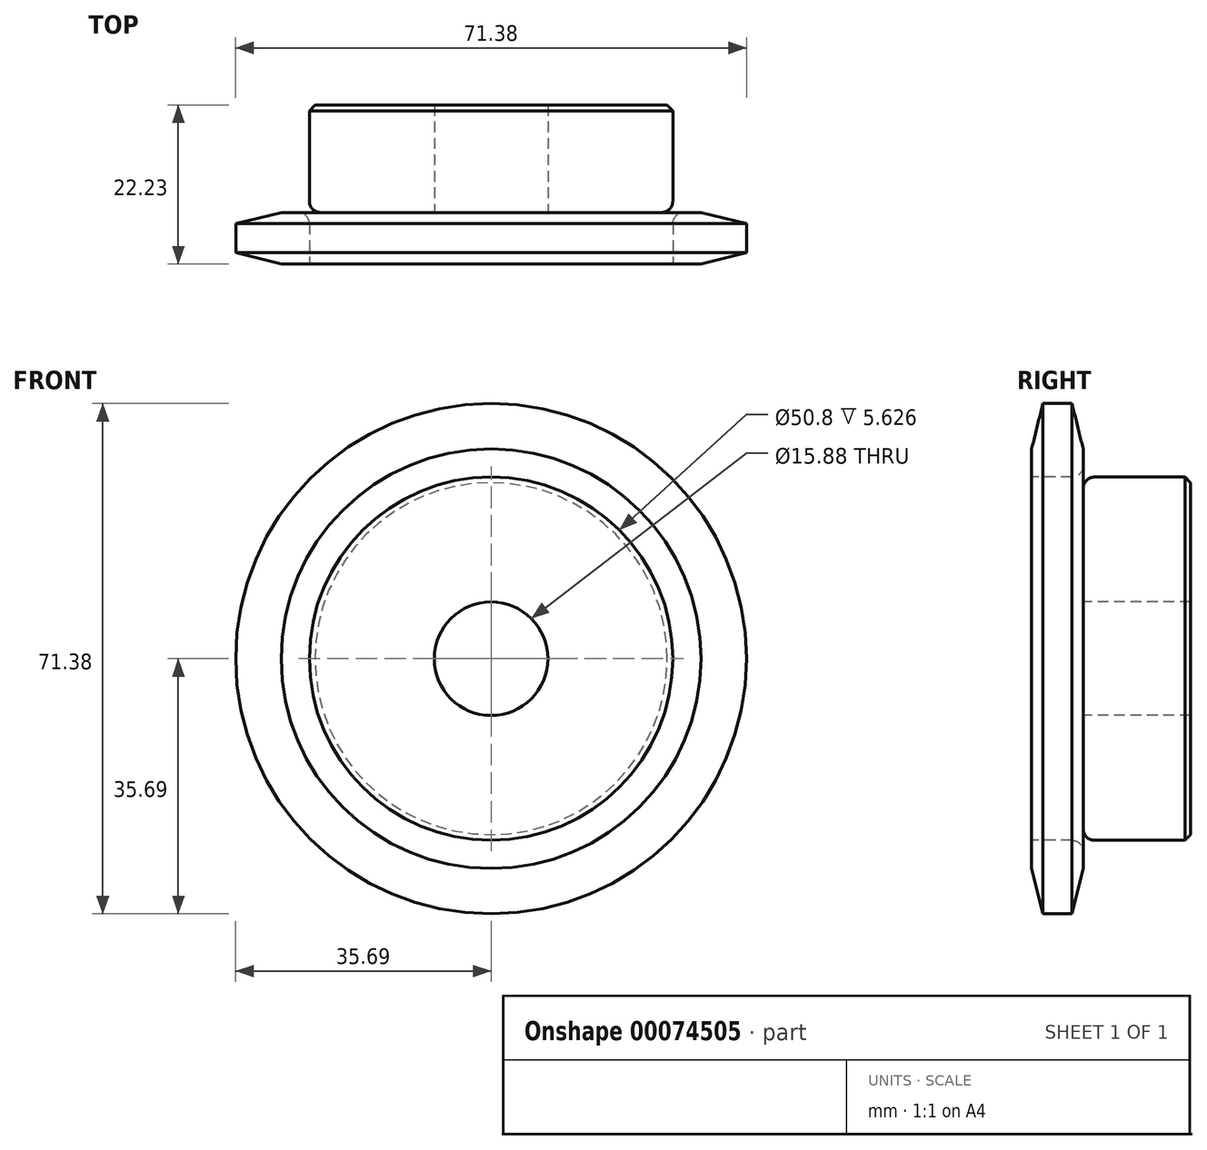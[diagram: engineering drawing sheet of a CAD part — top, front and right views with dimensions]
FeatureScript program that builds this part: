
annotation { "Feature Type Name" : "Feature", "Feature Type Description" : "" }
export const myFeature = defineFeature(function(context is Context, id is Id, definition is map)
    precondition{}
    {
        {
            var Q0;
            Q0=qCreatedBy(makeId("Right.planeOp"),FACE);
            var sketch = newSketch(context, id + "F0", { "sketchPlane" : qUnion([Q0])});
            skLineSegment(sketch, "E0", {"start": v(-33.01, 0) * mm, "end": v(15.45, 0) * mm, "construction": true});
            skLineSegment(sketch, "E1.bottom", {"start": v(0, 35.69) * mm, "end": v(7.21, 35.69) * mm});
            skLineSegment(sketch, "E1.top", {"start": v(0, 7.94) * mm, "end": v(7.21, 7.94) * mm});
            skLineSegment(sketch, "E1.left", {"start": v(0, 35.69) * mm, "end": v(0, 7.94) * mm});
            skLineSegment(sketch, "E1.right", {"start": v(7.21, 35.69) * mm, "end": v(7.21, 7.94) * mm});
            skLineSegment(sketch, "E2.bottom", {"start": v(0, 7.94) * mm, "end": v(22.23, 7.94) * mm});
            skLineSegment(sketch, "E2.top", {"start": v(0, 25.4) * mm, "end": v(22.23, 25.4) * mm});
            skLineSegment(sketch, "E2.left", {"start": v(0, 7.94) * mm, "end": v(0, 25.4) * mm});
            skLineSegment(sketch, "E2.right", {"start": v(22.22, 7.94) * mm, "end": v(22.22, 25.4) * mm});
            skLineSegment(sketch, "E3.MirrorCS", {"start": v(0, -7.94) * mm, "end": v(7.21, -7.94) * mm});
            skLineSegment(sketch, "E4.MirrorCS", {"start": v(22.23, -7.94) * mm, "end": v(22.23, -25.4) * mm});
            skLineSegment(sketch, "E5.MirrorCS", {"start": v(0, -7.94) * mm, "end": v(0, -25.4) * mm});
            skLineSegment(sketch, "E6.MirrorCS", {"start": v(0, -35.69) * mm, "end": v(7.21, -35.69) * mm});
            skLineSegment(sketch, "E7.MirrorCS", {"start": v(0, -35.69) * mm, "end": v(0, -7.94) * mm});
            skLineSegment(sketch, "E8.MirrorCS", {"start": v(7.21, -35.69) * mm, "end": v(7.21, -7.94) * mm});
            skLineSegment(sketch, "E9.MirrorCS", {"start": v(0, -7.94) * mm, "end": v(22.23, -7.94) * mm});
            skLineSegment(sketch, "E10.MirrorCS", {"start": v(0, -25.4) * mm, "end": v(22.23, -25.4) * mm});
            skSolve(sketch);
        }
        {
            var Q0;
            {var subQ0=sQuery(id+"F0.wireOp",EDGE,"E1.bottom");Q0=makeQuery(id+"F0.imprint","IMPRINT",FACE,{"disambiguationData":[TD([[makeQuery(id+"F0.imprint","IMPRINT",EDGE,{"derivedFrom":subQ0}),-1.0]])]});}
            var Q1;
            {var subQ5=sQuery(id+"F0.wireOp",EDGE,"E2.left");Q1=makeQuery(id+"F0.imprint","IMPRINT",FACE,{"disambiguationData":[TD([[makeQuery(id+"F0.imprint","IMPRINT",EDGE,{"derivedFrom":subQ5}),-1.0]])]});}
            var Q2;
            {var subQ5=sQuery(id+"F0.wireOp",EDGE,"E2.right");Q2=makeQuery(id+"F0.imprint","IMPRINT",FACE,{"disambiguationData":[TD([[makeQuery(id+"F0.imprint","IMPRINT",EDGE,{"derivedFrom":subQ5}),1.0]])]});}
            var Q3;
            Q3=sQuery(id+"F0.wireOp",EDGE,"E0");
            revolve(context, id + "F1", {"entities" : qUnion([Q0, Q1, Q2]), "axis" : qUnion([Q3]), "revolveType" : RevolveType.FULL});
        }
        {
            var Q0;
            Q0=makeQuery(id+"F1.opRevolve","SWEPT_EDGE",EDGE,{"disambiguationData":[OSD([sQuery(id+"F0.wireOp",EDGE,"E1.right"),sQuery(id+"F0.wireOp",EDGE,"E2.top")])]});
            fillet(context, id + "F2", {"entities" : qUnion([Q0]), "radius" : 1.59 * mm, "tangentPropagation" : true, "allowEdgeOverflow" : false});
        }
        {
            var Q0;
            Q0=makeQuery(id+"F1.opRevolve","SWEPT_EDGE",EDGE,{"disambiguationData":[OSD([sQuery(id+"F0.wireOp",EDGE,"E2.top"),sQuery(id+"F0.wireOp",EDGE,"E2.right")])]});
            chamfer(context, id + "F3", {"entities" : qUnion([Q0]), "width" : 0.8 * mm, "tangentPropagation" : true});
        }
        {
            var Q0;
            Q0=makeQuery(id+"F1.opRevolve","SWEPT_EDGE",EDGE,{"disambiguationData":[OSD([sQuery(id+"F0.wireOp",EDGE,"E1.bottom"),sQuery(id+"F0.wireOp",EDGE,"E1.left")])]});
            var Q1;
            Q1=makeQuery(id+"F1.opRevolve","SWEPT_EDGE",EDGE,{"disambiguationData":[OSD([sQuery(id+"F0.wireOp",EDGE,"E1.bottom"),sQuery(id+"F0.wireOp",EDGE,"E1.right")])]});
            chamfer(context, id + "F4", {"entities" : qUnion([Q0, Q1]), "chamferType" : ChamferType.TWO_OFFSETS, "width1" : 6.35 * mm, "oppositeDirection" : false, "width2" : 1.57 * mm, "tangentPropagation" : true});
        }
    });
